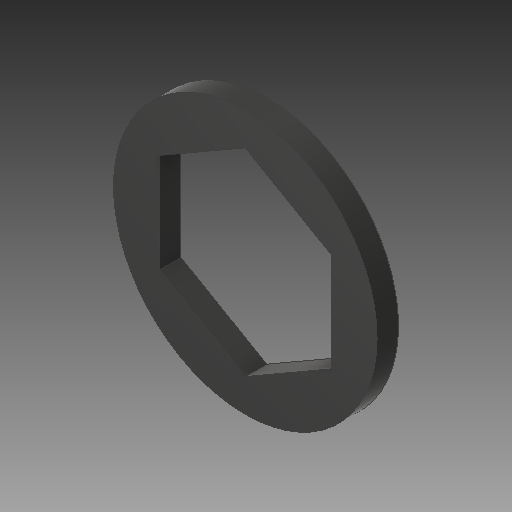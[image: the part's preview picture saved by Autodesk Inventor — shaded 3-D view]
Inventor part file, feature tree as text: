
AUTODESK INVENTOR PART (.ipt)
format: ipt  version: 2018 (Build 220112000, 112)  size: 94,720 bytes
history: native  units: in
note: dims shown in document units (in); Inventor stores cm internally (conversion verified against a paired STEP export)
features: extrude x1, sketch x1
ambient origin geometry x8: Origin, YZ Plane, XZ Plane, XY Plane, X Axis, Y Axis, Z Axis, Center Point
bodies: Solid1 (feature_tree)
feature tree (2):
  extrude  "Extrusion1"  Depth=0.0625in
  sketch  "Sketch1"  dims[d0=0.5in d1=0.768in d2=0.0625in d3=0.0in]
